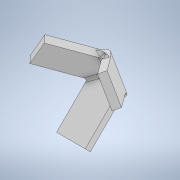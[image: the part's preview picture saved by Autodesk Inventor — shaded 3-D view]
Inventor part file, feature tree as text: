
AUTODESK INVENTOR PART (.ipt)
format: ipt  version: 2020 (Build 240168000, 168)  size: 280,576 bytes
history: native  units: mm
features: extrude x11, sketch x11, projected_geometry x8, fillet x3, pattern_circular x1, chamfer x1
ambient origin geometry x8: Origin, YZ Plane, XZ Plane, XY Plane, X Axis, Y Axis, Z Axis, Center Point
bodies: Solid1 (feature_tree)
feature tree (35):
  extrude  "Extrusion1"  Depth=20.0mm
  extrude  "Extrusion2"  Depth=5.0mm
  extrude  "Extrusion3"  Depth=20.0mm
  extrude  "Extrusion4"  Depth=5.0mm
  extrude  "Extrusion5"  Depth=5.0mm
  extrude  "Extrusion6"  Depth=20.0mm
  extrude  "Extrusion7"  Depth=20.0mm TaperAngle=0.0deg
  pattern_circular  "Circular Pattern1"  Count=2  [1 undecoded]
  extrude  "Extrusion8"  Depth=20.0mm
  fillet  "Fillet1"  Radius=20.0mm
  fillet  "Fillet2"  Radius=20.0mm
  fillet  "Fillet3"  Radius=20.0mm
  chamfer  "Chamfer1"  Distance=5.0mm
  extrude  "Extrusion9"  Depth=5.0mm TaperAngle=0.0deg
  extrude  "Extrusion10"  Depth=2.0mm
  extrude  "Extrusion11"  Depth=2.0mm
  sketch  "Sketch1"  dims[d0=20.0mm d1=20.0mm]
  sketch  "Sketch2"  dims[d2=60.0deg d3=5.0mm]
  projected_geometry  "Projected Loop1"
  sketch  "Sketch3"  dims[d4=20.0mm d5=20.0mm]
  projected_geometry  "Projected Loop2"
  sketch  "Sketch4"  dims[d6=5.0mm d7=5.0mm]
  projected_geometry  "Projected Loop3"
  sketch  "Sketch5"  dims[d8=20.0mm d9=5.0mm]
  projected_geometry  "Projected Loop4"
  sketch  "Sketch6"  dims[d10=3.0mm d11=0.0mm d12=20.0mm]
  projected_geometry  "Projected Loop5"
  sketch  "Sketch7"  dims[d13=20.0mm d14=20.0mm d15=0.0mm d16=20.0mm d17=0.0mm]
  sketch  "Sketch8"  dims[d18=5.0mm d19=35.0mm d20=20.0mm d21=0.0mm d22=20.0mm d23=0.0mm d24=20.0mm d25=0.0mm]
  sketch  "Sketch9"  dims[d26=3.0mm d27=5.0mm d28=0.0mm]
  projected_geometry  "Projected Loop6"
  sketch  "Sketch10"  dims[d29=30.0mm d30=360.0deg d32=5.0mm d33=0.0mm]
  projected_geometry  "Projected Loop7"
  sketch  "Sketch11"  dims[d34=1.0mm d35=2.0mm d36=2.0mm d37=3.0mm d38=2.0mm d39=45.0deg d40=5.0mm d41=0.0mm d42=5.0mm d43=0.0mm d44=5.0mm d45=0.0mm]
  projected_geometry  "Projected Loop8"
note: 1 required parameter value undecoded (feature->parameter linkage not recoverable at this tier; creation-order binding heuristic only, values carry confidence <= 0.55)
